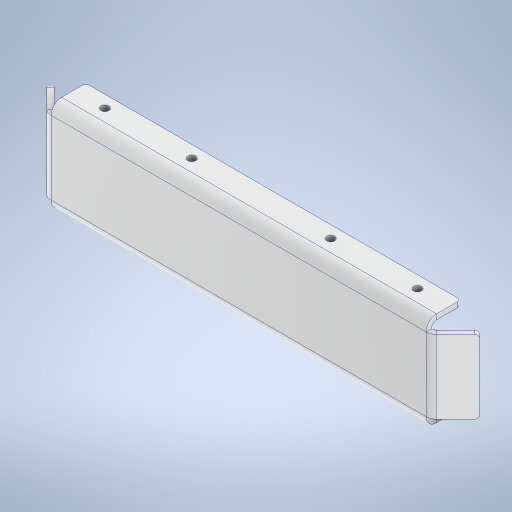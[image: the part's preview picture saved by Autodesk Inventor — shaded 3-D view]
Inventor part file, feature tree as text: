
AUTODESK INVENTOR PART (.ipt)
format: ipt  version: 2024 (Build 280153000, 153)  size: 379,904 bytes
history: native  units: mm
features: other x9, sketch x4, extrude x2, fillet x1
ambient origin geometry x8: Origin, YZ Plane, XZ Plane, XY Plane, X Axis, Y Axis, Z Axis, Center Point
bodies: Volumenkörper1 (feature_tree)
feature tree (16):
  extrude  "Extrusion1"  Depth=42.3mm
  other  "Lasche1"
  other  "Lasche2"
  extrude  "Extrusion2"  Depth=3.0mm
  fillet  "Rundung1"  Radius=3.0mm
  sketch  "Skizze1"  dims[d0=216.0mm d1=42.3mm]
  sketch  "Skizze2"  dims[d2=3.0mm d3=0.0mm d4=3.0mm d5=3.0mm]
  other  "Grobblech1"
  other  "Biegung1"
  other  "Ecke1"
  sketch  "Skizze3"  dims[d6=1.5mm]
  other  "Grobblech2"
  other  "Biegung2"
  other  "Ecke2"
  sketch  "Skizze4"  dims[d7=6.0mm d8=3.0mm d9=20.0mm d10=90.0deg d11=3.0mm d12=12.0mm d13=3.0mm d14=3.0mm d15=3.0mm d16=1.5mm d17=6.0mm d18=3.0mm d19=20.0mm d20=45.0deg d21=3.0mm d22=12.0mm d23=3.0mm d24=3.0mm d25=4.5mm d26=4.5mm d27=4.5mm d28=4.5mm d29=80.0mm d30=180.0mm d31=100.0mm d32=0.0mm d33=2.0mm]
  other  "Definition1"
